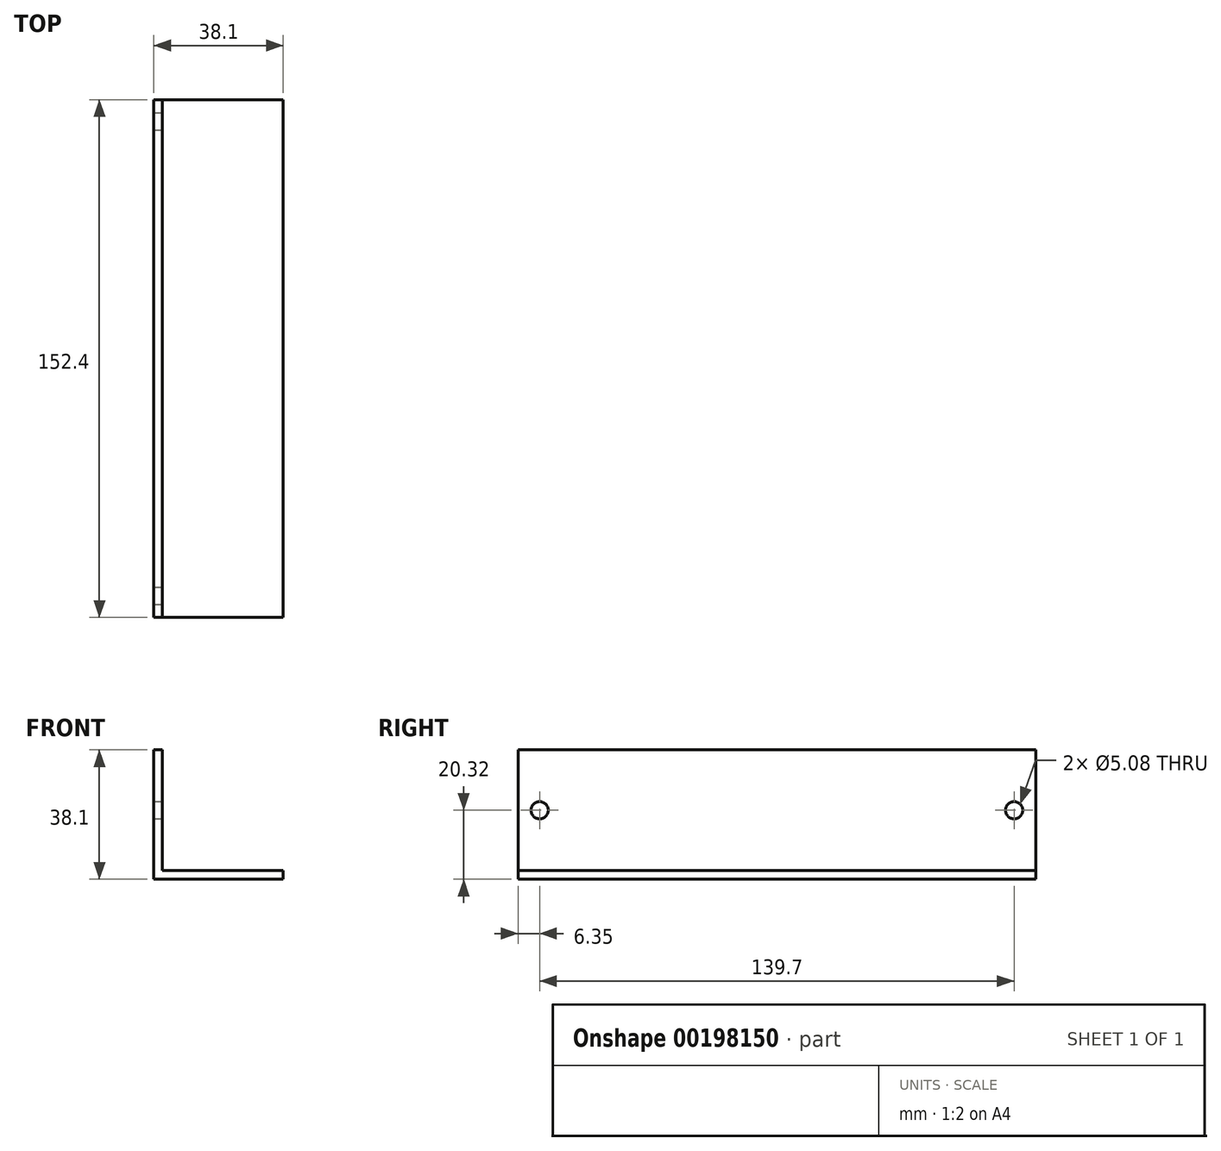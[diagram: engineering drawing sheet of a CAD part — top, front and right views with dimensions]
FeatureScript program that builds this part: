
annotation { "Feature Type Name" : "Feature", "Feature Type Description" : "" }
export const myFeature = defineFeature(function(context is Context, id is Id, definition is map)
    precondition{}
    {
        {
            var Q0;
            Q0=qCreatedBy(makeId("Front.planeOp"),FACE);
            var sketch = newSketch(context, id + "F0", { "sketchPlane" : qUnion([Q0])});
            skLineSegment(sketch, "E0", {"start": v(0, 0) * mm, "end": v(0, 2.54) * mm});
            skLineSegment(sketch, "E1", {"start": v(0, 2.54) * mm, "end": v(-35.56, 2.54) * mm});
            skLineSegment(sketch, "E2", {"start": v(-35.56, 2.54) * mm, "end": v(-35.56, 38.1) * mm});
            skLineSegment(sketch, "E3", {"start": v(-35.56, 38.1) * mm, "end": v(-38.1, 38.1) * mm});
            skLineSegment(sketch, "E4", {"start": v(-38.1, 38.1) * mm, "end": v(-38.1, 0) * mm});
            skLineSegment(sketch, "E5", {"start": v(-38.1, 0) * mm, "end": v(0, 0) * mm});
            skSolve(sketch);
        }
        {
            var Q0;
            Q0 = qSketchRegion(id + "F0", true);
            extrude(context, id + "F1", {"entities" : qUnion([Q0]), "oppositeDirection" : true, "depth" : 152.4 * mm});
        }
        {
            var Q0;
            Q0=makeQuery(id+"F1.opExtrude","SWEPT_FACE",FACE,{"disambiguationData":[OSD([sQuery(id+"F0.wireOp",EDGE,"E2")])]});
            var sketch = newSketch(context, id + "F2", { "sketchPlane" : qUnion([Q0])});
            skLineSegment(sketch, "E6", {"start": v(0, 20.32) * mm, "end": v(3.81, 20.32) * mm});
            skCircle(sketch, "E7", {"center": v(6.35, 20.32) * mm, "radius": 2.54 * mm});
            skLineSegment(sketch, "E8.trimOffspring", {"start": v(31.62, 20.32) * mm, "end": v(76.53, 20.32) * mm});
            skLineSegment(sketch, "E9.trimOffspring", {"start": v(8.9, 20.32) * mm, "end": v(26.54, 20.32) * mm});
            skLineSegment(sketch, "E10", {"start": v(76.2, 38.1) * mm, "end": v(76.2, 2.54) * mm});
            skCircle(sketch, "E11.MirrorC", {"center": v(146.05, 20.32) * mm, "radius": 2.54 * mm});
            skSolve(sketch);
        }
        {
            var Q0;
            Q0 = qSketchRegion(id + "F2", true);
            extrude(context, id + "F3", {"entities" : qUnion([Q0]), "operationType" : NewBodyOperationType.REMOVE, "oppositeDirection" : true, "depth" : 25.4 * mm});
        }
    });
